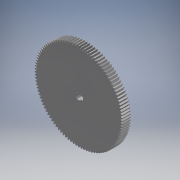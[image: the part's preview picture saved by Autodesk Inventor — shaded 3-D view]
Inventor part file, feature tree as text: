
AUTODESK INVENTOR PART (.ipt)
format: ipt  version: 2019 (Build 230136000, 136)  size: 606,208 bytes
history: native  units: mm (DEFAULTED — no unit token found)
features: other x5, sketch x5, extrude x4, plane x3, fillet x1
ambient origin geometry x8: Origin, YZ Plane, XZ Plane, XY Plane, X Axis, Y Axis, Z Axis, Center Point
bodies: Solid1 (feature_tree)
feature tree (18):
  extrude  "Extrusion1"  Depth=6.35mm TaperAngle=0.0deg
  plane  "Work Plane1"
  plane  "Work Plane2"
  plane  "Work Plane3"
  other  "Spur Gear"
  sketch  "Sketch3"  dims[d6=0.0mm d7=0.302076mm d9=0.0mm]
  extrude  "Extrusion2"  Depth=76.2mm TaperAngle=0.0deg
  extrude  "Extrusion3"  TaperAngle=0.0deg  [1 undecoded]
  other  "Keyway1"
  extrude  "Extrusion4"  TaperAngle=0.0deg  [1 undecoded]
  fillet  "Fillet1"  Radius=12.7mm
  sketch  "Sketch1"  dims[d0=68.36947mm d1=6.35mm d2=0.0mm]
  sketch  "Sketch2"  dims[d3=67.107183mm d4=76.2mm d5=0.0mm]
  other  "Srf1"
  other  "Hub Keyway"
  sketch  "Sketch4"  dims[d14=0.0mm d15=37.74779mm d16=0.0mm]
  sketch  "Sketch5"  dims[d17=0.0mm d18=0.0mm d19=37.74779mm d20=12.7mm d21=4.445mm d22=0.0mm d23=7.999984mm d24=6.985mm d25=0.0mm d26=6.985mm d27=0.0mm d28=3.175mm]
  other  "Pitch Diameter"
note: 2 required parameter values undecoded (feature->parameter linkage not recoverable at this tier; creation-order binding heuristic only, values carry confidence <= 0.55)
